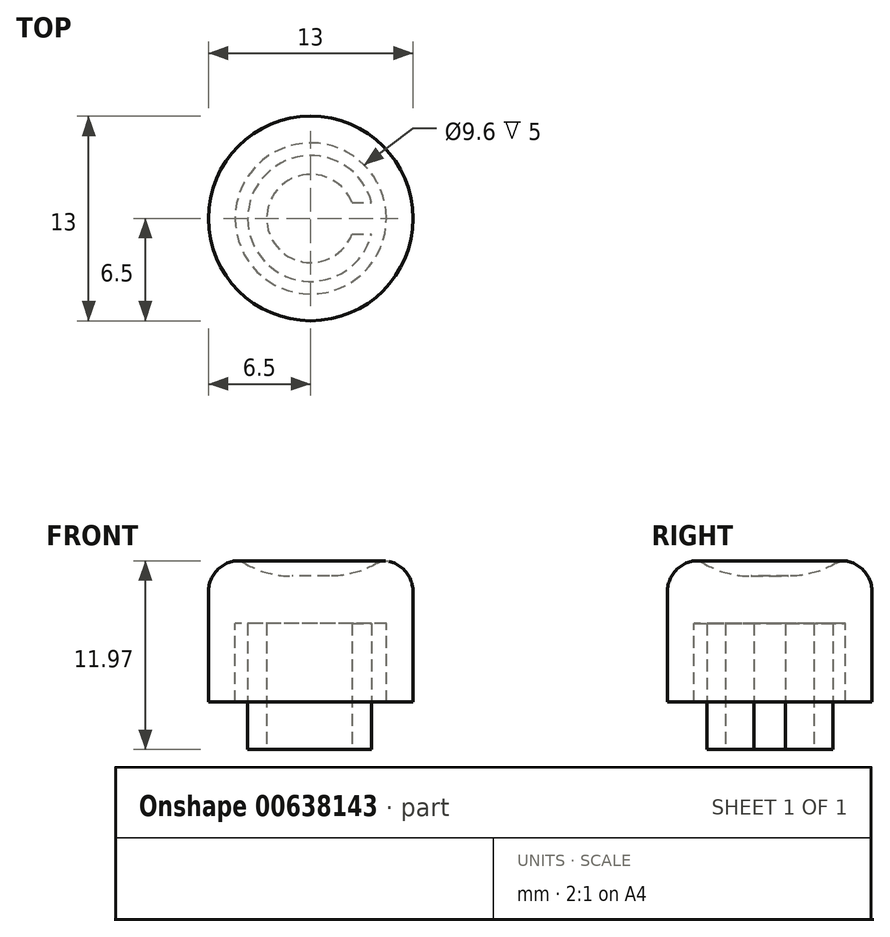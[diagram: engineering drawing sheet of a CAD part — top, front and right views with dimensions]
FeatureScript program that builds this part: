
annotation { "Feature Type Name" : "Feature", "Feature Type Description" : "" }
export const myFeature = defineFeature(function(context is Context, id is Id, definition is map)
    precondition{}
    {
        {
            var Q0;
            Q0=qCreatedBy(makeId("Top.planeOp"),FACE);
            var sketch = newSketch(context, id + "F0", { "sketchPlane" : qUnion([Q0])});
            skCircle(sketch, "E0", {"center": v(0, 0) * mm, "radius": 2.8 * mm});
            skCircle(sketch, "E1", {"center": v(0, 0) * mm, "radius": 4 * mm});
            skSolve(sketch);
        }
        {
            var Q0;
            Q0=makeQuery(id+"F0.imprint","IMPRINT",FACE,{"disambiguationData":[TD([[makeQuery(id+"F0.imprint","IMPRINT",EDGE,{"derivedFrom":sQuery(id+"F0.wireOp",EDGE,"E0")}),-1.0]])]});
            extrude(context, id + "F1", {"entities" : qUnion([Q0]), "depth" : 8 * mm, "offsetDistance" : 25 * mm});
        }
        {
            var Q0;
            Q0=makeQuery(id+"F1.opExtrude","CAP_FACE",FACE,{"disambiguationData":[OSD([sQuery(id+"F0.wireOp",EDGE,"E0"),sQuery(id+"F0.wireOp",EDGE,"E1")])],"isStart":false});
            var sketch = newSketch(context, id + "F2", { "sketchPlane" : qUnion([Q0])});
            skCircle(sketch, "E2", {"center": v(0, 0) * mm, "radius": 6.5 * mm});
            skCircle(sketch, "E3", {"center": v(0, 0) * mm, "radius": 4.8 * mm});
            skSolve(sketch);
        }
        {
            var Q0;
            Q0=makeQuery(id+"F2.imprint","IMPRINT",FACE,{"disambiguationData":[TD([[makeQuery(id+"F2.imprint","IMPRINT",EDGE,{"derivedFrom":sQuery(id+"F2.wireOp",EDGE,"E2")}),1.0]])]});
            var Q1;
            Q1=makeQuery(id+"F2.imprint","IMPRINT",FACE,{"disambiguationData":[TD([[makeQuery(id+"F2.imprint","IMPRINT",EDGE,{"derivedFrom":makeQuery(id+"F1.opExtrude","CAP_EDGE",EDGE,{"disambiguationData":[OSD([sQuery(id+"F0.wireOp",EDGE,"E0")])],"isStart":false})}),-1.0]])]});
            var Q2;
            Q2=makeQuery(id+"F2.imprint","IMPRINT",FACE,{"disambiguationData":[TD([[makeQuery(id+"F2.imprint","IMPRINT",EDGE,{"derivedFrom":makeQuery(id+"F1.opExtrude","CAP_EDGE",EDGE,{"disambiguationData":[OSD([sQuery(id+"F0.wireOp",EDGE,"E0")])],"isStart":false})}),1.0]])]});
            var Q3;
            Q3=makeQuery(id+"F2.imprint","IMPRINT",FACE,{"disambiguationData":[TD([[makeQuery(id+"F2.imprint","IMPRINT",EDGE,{"derivedFrom":sQuery(id+"F2.wireOp",EDGE,"E3")}),1.0]])]});
            extrude(context, id + "F3", {"entities" : qUnion([Q0, Q1, Q2, Q3]), "depth" : 4 * mm, "offsetDistance" : 25 * mm});
        }
        {
            var Q0;
            Q0=makeQuery(id+"F3.opExtrude","CAP_EDGE",EDGE,{"disambiguationData":[OSD([sQuery(id+"F2.wireOp",EDGE,"E2")])],"isStart":false});
            fillet(context, id + "F4", {"entities" : qUnion([Q0]), "radius" : 2 * mm, "tangentPropagation" : true, "allowEdgeOverflow" : false});
        }
        {
            var Q0;
            Q0 = qSketchRegion(id + "F2", true);
            extrude(context, id + "F5", {"entities" : qUnion([Q0]), "operationType" : NewBodyOperationType.ADD, "oppositeDirection" : true, "depth" : 5 * mm, "offsetDistance" : 25 * mm});
        }
        {
            var Q0;
            Q0=makeQuery(id+"F1.opExtrude","CAP_FACE",FACE,{"disambiguationData":[OSD([sQuery(id+"F0.wireOp",EDGE,"E0"),sQuery(id+"F0.wireOp",EDGE,"E1")])],"isStart":true});
            var sketch = newSketch(context, id + "F6", { "sketchPlane" : qUnion([Q0])});
            skLineSegment(sketch, "E4.bottom", {"start": v(2.2, -1) * mm, "end": v(4.2, -1) * mm});
            skLineSegment(sketch, "E4.top", {"start": v(2.2, 1) * mm, "end": v(4.2, 1) * mm});
            skLineSegment(sketch, "E4.left", {"start": v(2.2, -1) * mm, "end": v(2.2, 1) * mm});
            skLineSegment(sketch, "E4.right", {"start": v(4.2, -1) * mm, "end": v(4.2, 1) * mm});
            skPoint(sketch, "E4.middle", {"position": v(3.2, 0) * mm});
            skSolve(sketch);
        }
        {
            var Q0;
            {var subQ0=sQuery(id+"F6.wireOp",EDGE,"E4.right");Q0=makeQuery(id+"F6.imprint","IMPRINT",FACE,{"disambiguationData":[TD([[makeQuery(id+"F6.imprint","IMPRINT",EDGE,{"derivedFrom":subQ0}),1.0]])]});}
            var Q1;
            {var subQ0=sQuery(id+"F6.wireOp",EDGE,"E4.bottom");var subQ1=makeQuery(id+"F1.opExtrude","CAP_EDGE",EDGE,{"disambiguationData":[OSD([sQuery(id+"F0.wireOp",EDGE,"E1")])],"isStart":true});var subQ2=makeQuery(id+"F6.imprint","INTERSECT",VERTEX,{"derivedFrom":[subQ1,subQ0]});Q1=makeQuery(id+"F6.imprint","IMPRINT",FACE,{"disambiguationData":[TD([[makeQuery(id+"F6.imprint","IMPRINT",EDGE,{"disambiguationData":[TD([[subQ2,1.0]])],"derivedFrom":subQ0}),1.0]])]});}
            var Q2;
            {var subQ0=sQuery(id+"F6.wireOp",EDGE,"E4.left");Q2=makeQuery(id+"F6.imprint","IMPRINT",FACE,{"disambiguationData":[TD([[makeQuery(id+"F6.imprint","IMPRINT",EDGE,{"derivedFrom":subQ0}),-1.0]])]});}
            extrude(context, id + "F7", {"entities" : qUnion([Q0, Q1, Q2]), "operationType" : NewBodyOperationType.REMOVE, "oppositeDirection" : true, "depth" : 8 * mm, "offsetDistance" : 25 * mm});
        }
        {
            var Q0;
            Q0=makeQuery(id+"F3.opExtrude","CAP_FACE",FACE,{"disambiguationData":[OSD([sQuery(id+"F2.wireOp",EDGE,"E2")])],"isStart":false});
            extrude(context, id + "F8", {"entities" : qUnion([Q0]), "operationType" : NewBodyOperationType.REMOVE, "oppositeDirection" : true, "depth" : 1 * mm, "offsetDistance" : 25 * mm});
        }
        {
            var Q0;
            Q0=makeQuery(id+"F8.boolean.opBoolean","COPY",EDGE,{"derivedFrom":makeQuery(id+"F8.opExtrude","CAP_EDGE",EDGE,{"disambiguationData":[OSD([sQuery(id+"F2.wireOp",EDGE,"E2")])],"isStart":false})});
            fillet(context, id + "F9", {"entities" : qUnion([Q0]), "radius" : 6 * mm, "tangentPropagation" : true, "allowEdgeOverflow" : false});
        }
        {
            var Q0;
            {var subQ0=sQuery(id+"F2.wireOp",EDGE,"E2");Q0=makeQuery(id+"F9.opFillet","BLEND_EDGE",EDGE,{"blendedFrom":[makeQuery(id+"F8.boolean.opBoolean","COPY",EDGE,{"derivedFrom":makeQuery(id+"F8.opExtrude","CAP_EDGE",EDGE,{"disambiguationData":[OSD([subQ0])],"isStart":false})}),makeQuery(id+"F4.opFillet","BLEND_FACE",FACE,{"disambiguationData":[OSD([subQ0])]})],"blendedInto":[makeQuery(id+"F4.opFillet","BLEND_FACE",FACE,{"disambiguationData":[OSD([subQ0])]})]});}
            fillet(context, id + "F10", {"entities" : qUnion([Q0]), "radius" : 1 * mm, "tangentPropagation" : true, "allowEdgeOverflow" : false});
        }
    });
